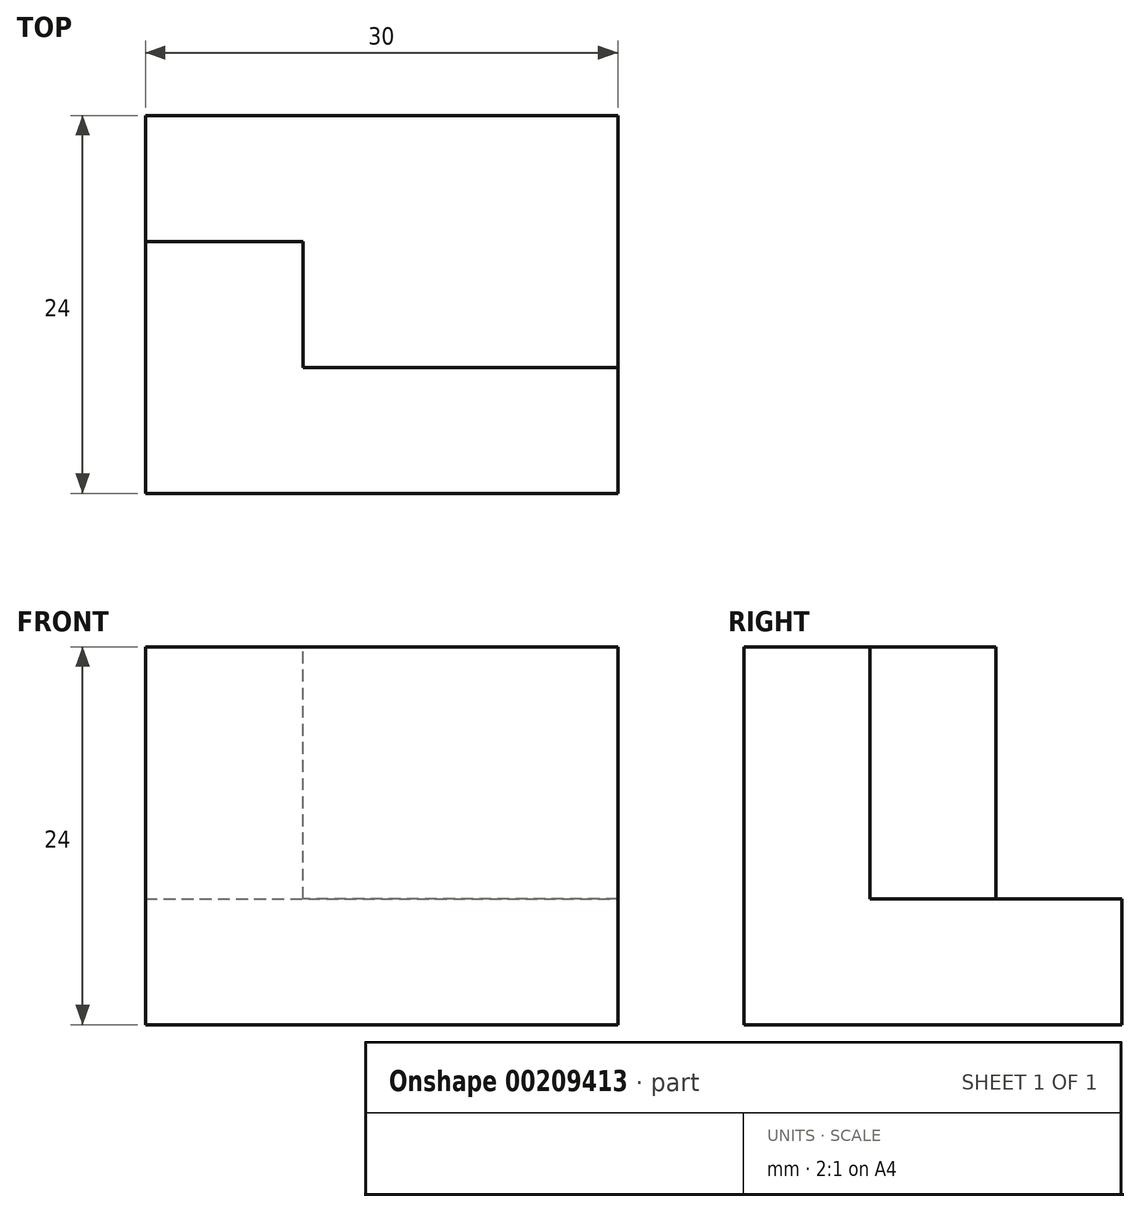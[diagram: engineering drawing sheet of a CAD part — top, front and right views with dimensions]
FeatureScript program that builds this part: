
annotation { "Feature Type Name" : "Feature", "Feature Type Description" : "" }
export const myFeature = defineFeature(function(context is Context, id is Id, definition is map)
    precondition{}
    {
        {
            var Q0;
            Q0=qCreatedBy(makeId("Top.planeOp"),FACE);
            var sketch = newSketch(context, id + "F0", { "sketchPlane" : qUnion([Q0])});
            skLineSegment(sketch, "E0.bottom", {"start": v(0, 0) * mm, "end": v(30, 0) * mm});
            skLineSegment(sketch, "E0.top", {"start": v(0, 24) * mm, "end": v(30, 24) * mm});
            skLineSegment(sketch, "E0.left", {"start": v(0, 0) * mm, "end": v(0, 24) * mm});
            skLineSegment(sketch, "E0.right", {"start": v(30, 0) * mm, "end": v(30, 24) * mm});
            skSolve(sketch);
        }
        {
            var Q0;
            Q0=makeQuery(id+"F0.imprint","IMPRINT",FACE,{"disambiguationData":[TD([[makeQuery(id+"F0.imprint","IMPRINT",EDGE,{"derivedFrom":sQuery(id+"F0.wireOp",EDGE,"E0.bottom")}),1.0]])]});
            extrude(context, id + "F1", {"entities" : qUnion([Q0]), "oppositeDirection" : true, "depth" : 24 * mm});
        }
        {
            var Q0;
            Q0=makeQuery(id+"F1.opExtrude","CAP_FACE",FACE,{"disambiguationData":[OSD([sQuery(id+"F0.wireOp",EDGE,"E0.bottom"),sQuery(id+"F0.wireOp",EDGE,"E0.top"),sQuery(id+"F0.wireOp",EDGE,"E0.left"),sQuery(id+"F0.wireOp",EDGE,"E0.right")])],"isStart":true});
            var sketch = newSketch(context, id + "F2", { "sketchPlane" : qUnion([Q0])});
            skLineSegment(sketch, "E1", {"start": v(0, 0) * mm, "end": v(30, 0) * mm});
            skLineSegment(sketch, "E2", {"start": v(30, 0) * mm, "end": v(30, 8) * mm});
            skLineSegment(sketch, "E3", {"start": v(30, 8) * mm, "end": v(0, 8) * mm});
            skLineSegment(sketch, "E4", {"start": v(0, 8) * mm, "end": v(0, 0) * mm});
            skLineSegment(sketch, "E5", {"start": v(0, 8) * mm, "end": v(0, 16) * mm});
            skLineSegment(sketch, "E6", {"start": v(0, 16) * mm, "end": v(10, 16) * mm});
            skLineSegment(sketch, "E7", {"start": v(10, 16) * mm, "end": v(10, 8) * mm});
            skPoint(sketch, "E8.start.orphan", {"position": v(10, 24) * mm});
            skSolve(sketch);
        }
        {
            var Q0;
            {var subQ0=sQuery(id+"F2.wireOp",EDGE,"E7");Q0=makeQuery(id+"F2.imprint","IMPRINT",FACE,{"disambiguationData":[TD([[makeQuery(id+"F2.imprint","IMPRINT",EDGE,{"derivedFrom":subQ0}),1.0]])]});}
            extrude(context, id + "F3", {"entities" : qUnion([Q0]), "operationType" : NewBodyOperationType.REMOVE, "oppositeDirection" : true, "depth" : 16 * mm});
        }
    });
